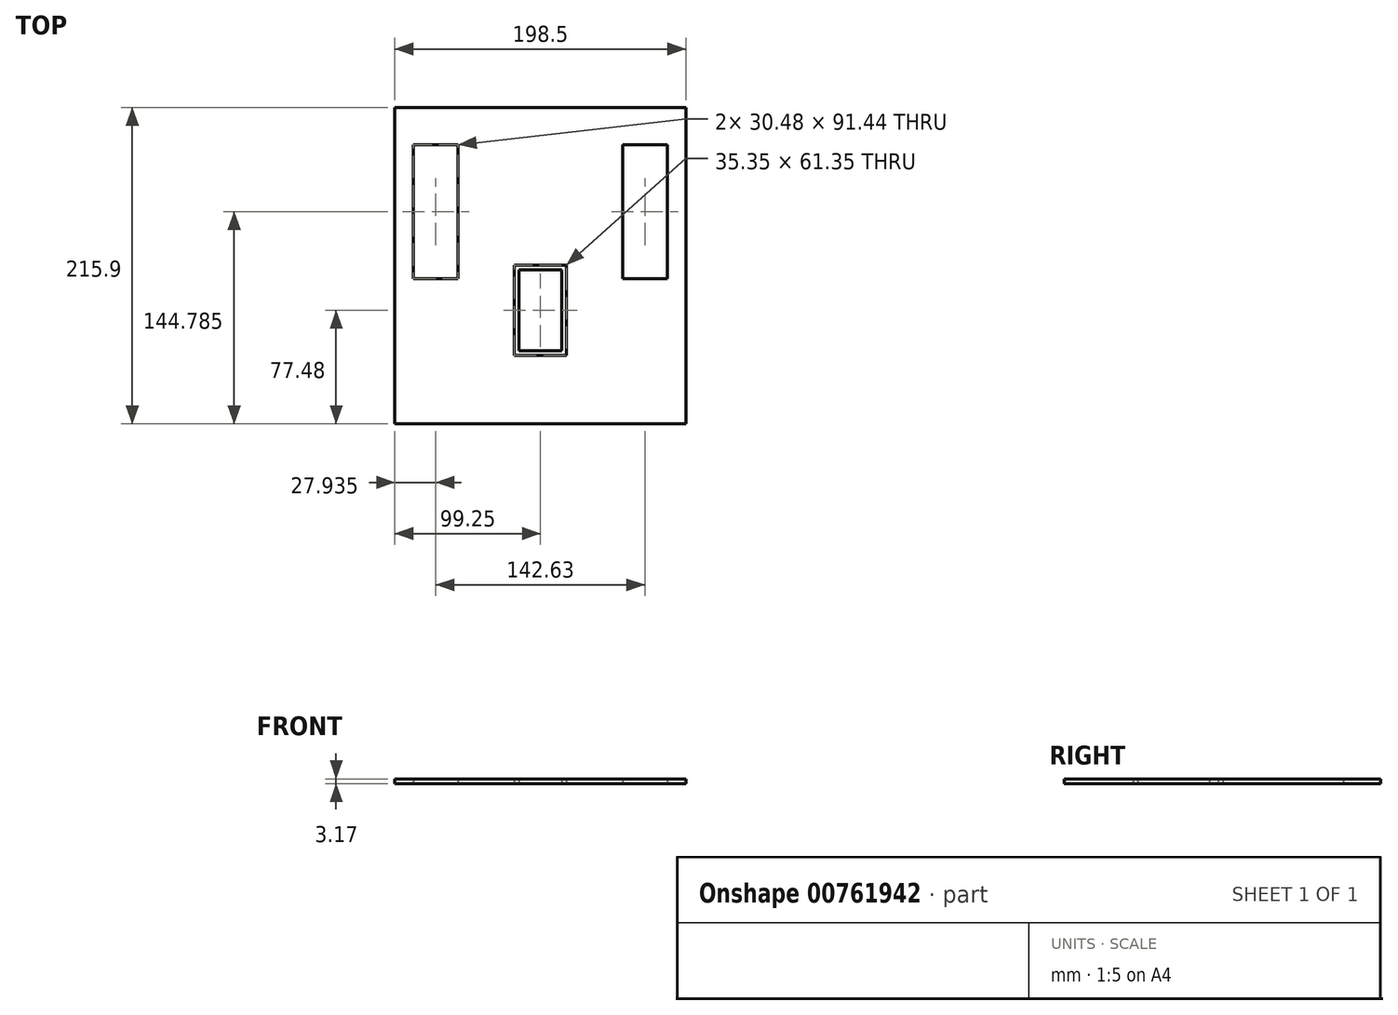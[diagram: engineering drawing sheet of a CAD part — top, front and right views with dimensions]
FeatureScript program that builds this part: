
annotation { "Feature Type Name" : "Feature", "Feature Type Description" : "" }
export const myFeature = defineFeature(function(context is Context, id is Id, definition is map)
    precondition{}
    {
        {
            var Q0;
            Q0=qCreatedBy(makeId("Top.planeOp"),FACE);
            var sketch = newSketch(context, id + "F0", { "sketchPlane" : qUnion([Q0])});
            skLineSegment(sketch, "E0", {"start": v(-27.5, 0) * mm, "end": v(-27.5, 38) * mm});
            skLineSegment(sketch, "E1", {"start": v(27.5, 38) * mm, "end": v(-27.5, 38) * mm});
            skLineSegment(sketch, "E2", {"start": v(27.5, 38) * mm, "end": v(27.5, -38) * mm});
            skLineSegment(sketch, "E3", {"start": v(27.5, -38) * mm, "end": v(-27.5, -38) * mm});
            skLineSegment(sketch, "E4", {"start": v(-27.5, 0) * mm, "end": v(-27.5, -38) * mm});
            skLineSegment(sketch, "E5", {"start": v(-30.68, 38) * mm, "end": v(-30.68, 41.18) * mm});
            skLineSegment(sketch, "E6", {"start": v(-30.68, 41.18) * mm, "end": v(-27.5, 41.18) * mm});
            skLineSegment(sketch, "E7", {"start": v(-27.5, -41.17) * mm, "end": v(-30.68, -41.17) * mm});
            skLineSegment(sketch, "E8", {"start": v(-30.68, -41.17) * mm, "end": v(-30.68, 38) * mm});
            skLineSegment(sketch, "E9", {"start": v(-27.5, 41.18) * mm, "end": v(27.5, 41.18) * mm});
            skLineSegment(sketch, "E10", {"start": v(27.5, 41.18) * mm, "end": v(30.68, 41.18) * mm});
            skLineSegment(sketch, "E11", {"start": v(30.68, -38) * mm, "end": v(30.68, 41.18) * mm});
            skLineSegment(sketch, "E12", {"start": v(30.68, -38) * mm, "end": v(30.68, -41.17) * mm});
            skLineSegment(sketch, "E13", {"start": v(30.68, -41.17) * mm, "end": v(-27.5, -41.17) * mm});
            skLineSegment(sketch, "E14", {"start": v(-27.5, -41.17) * mm, "end": v(27.5, -41.17) * mm});
            skLineSegment(sketch, "E15", {"start": v(-27.5, -41.17) * mm, "end": v(0, -41.17) * mm});
            skLineSegment(sketch, "E16", {"start": v(0, -41.17) * mm, "end": v(14.5, -41.17) * mm});
            skLineSegment(sketch, "E17", {"start": v(14.5, -41.17) * mm, "end": v(0, -41.17) * mm});
            skLineSegment(sketch, "E18", {"start": v(0, -41.17) * mm, "end": v(-13.75, -41.17) * mm});
            skLineSegment(sketch, "E19", {"start": v(0, -41.17) * mm, "end": v(-14.5, -41.17) * mm});
            skLineSegment(sketch, "E20", {"start": v(-14.5, -44.35) * mm, "end": v(-14.5, -96.17) * mm});
            skLineSegment(sketch, "E21", {"start": v(14.5, -96.17) * mm, "end": v(14.5, -44.35) * mm});
            skLineSegment(sketch, "E22", {"start": v(14.5, -96.17) * mm, "end": v(14.5, -99.35) * mm});
            skLineSegment(sketch, "E23", {"start": v(14.5, -99.35) * mm, "end": v(-14.5, -99.35) * mm});
            skLineSegment(sketch, "E24", {"start": v(-17.67, -99.35) * mm, "end": v(-17.67, -41.17) * mm});
            skLineSegment(sketch, "E25", {"start": v(14.5, -44.35) * mm, "end": v(-14.5, -44.35) * mm});
            skLineSegment(sketch, "E26", {"start": v(14.5, -41.17) * mm, "end": v(17.68, -41.17) * mm});
            skLineSegment(sketch, "E27", {"start": v(17.68, -99.35) * mm, "end": v(17.68, -41.17) * mm});
            skLineSegment(sketch, "E28", {"start": v(-17.67, -99.35) * mm, "end": v(-17.67, -102.53) * mm});
            skLineSegment(sketch, "E29", {"start": v(-17.67, -102.53) * mm, "end": v(17.68, -102.53) * mm});
            skLineSegment(sketch, "E30", {"start": v(17.68, -102.53) * mm, "end": v(17.68, -99.35) * mm});
            skLineSegment(sketch, "E31", {"start": v(-14.5, -96.17) * mm, "end": v(-14.5, -99.35) * mm});
            skLineSegment(sketch, "E32", {"start": v(-30.68, 41.18) * mm, "end": v(-56.08, 41.18) * mm});
            skLineSegment(sketch, "E33", {"start": v(-56.08, 41.18) * mm, "end": v(-86.55, 41.18) * mm});
            skLineSegment(sketch, "E34", {"start": v(-86.55, 41.18) * mm, "end": v(-86.55, -50.27) * mm});
            skLineSegment(sketch, "E35", {"start": v(-56.07, -50.27) * mm, "end": v(-86.55, -50.27) * mm});
            skLineSegment(sketch, "E36", {"start": v(-56.07, -50.27) * mm, "end": v(-56.08, 41.18) * mm});
            skLineSegment(sketch, "E37", {"start": v(30.68, 41.18) * mm, "end": v(56.08, 41.18) * mm});
            skLineSegment(sketch, "E38", {"start": v(56.08, 41.18) * mm, "end": v(86.56, 41.18) * mm});
            skLineSegment(sketch, "E39", {"start": v(86.56, 41.18) * mm, "end": v(86.56, -50.27) * mm});
            skLineSegment(sketch, "E40", {"start": v(86.56, -50.27) * mm, "end": v(56.08, -50.27) * mm});
            skLineSegment(sketch, "E41", {"start": v(56.08, -50.27) * mm, "end": v(56.08, 41.18) * mm});
            skLineSegment(sketch, "E42", {"start": v(-86.55, 41.18) * mm, "end": v(-86.55, 66.57) * mm});
            skLineSegment(sketch, "E43", {"start": v(-86.55, 66.57) * mm, "end": v(-86.55, 41.18) * mm});
            skLineSegment(sketch, "E44", {"start": v(86.56, 41.18) * mm, "end": v(86.56, 66.58) * mm});
            skLineSegment(sketch, "E45", {"start": v(86.56, 66.58) * mm, "end": v(99.26, 66.58) * mm});
            skLineSegment(sketch, "E46", {"start": v(-86.55, 66.57) * mm, "end": v(-99.26, 66.57) * mm});
            skLineSegment(sketch, "E47", {"start": v(-99.26, 66.57) * mm, "end": v(-99.26, -149.32) * mm});
            skLineSegment(sketch, "E48", {"start": v(-99.26, -149.32) * mm, "end": v(-99.26, 66.57) * mm});
            skLineSegment(sketch, "E49", {"start": v(99.26, 66.58) * mm, "end": v(99.26, -149.32) * mm});
            skLineSegment(sketch, "E50", {"start": v(99.26, -149.32) * mm, "end": v(-99.25, -149.32) * mm});
            skLineSegment(sketch, "E51", {"start": v(-86.55, 66.57) * mm, "end": v(86.56, 66.58) * mm});
            skSolve(sketch);
        }
        {
            var Q0;
            Q0 = qSketchRegion(id + "F0", true);
            var Q1;
            Q1=makeQuery(id+"F0.imprint","IMPRINT",FACE,{"disambiguationData":[TD([[makeQuery(id+"F0.imprint","IMPRINT",EDGE,{"derivedFrom":sQuery(id+"F0.wireOp",EDGE,"E0")}),-1.0]])]});
            var Q2;
            Q2=makeQuery(id+"F0.imprint","IMPRINT",FACE,{"disambiguationData":[TD([[makeQuery(id+"F0.imprint","IMPRINT",EDGE,{"derivedFrom":sQuery(id+"F0.wireOp",EDGE,"E20")}),1.0]])]});
            var Q3;
            {var subQ4=sQuery(id+"F0.wireOp",EDGE,"E17");Q3=makeQuery(id+"F0.imprint","IMPRINT",FACE,{"disambiguationData":[TD([[makeQuery(id+"F0.imprint","IMPRINT",EDGE,{"derivedFrom":subQ4}),1.0]])]});}
            var Q4;
            Q4=makeQuery(id+"F0.imprint","IMPRINT",FACE,{"disambiguationData":[TD([[makeQuery(id+"F0.imprint","IMPRINT",EDGE,{"derivedFrom":sQuery(id+"F0.wireOp",EDGE,"E0")}),1.0]])]});
            extrude(context, id + "F1", {"entities" : qUnion([Q0, Q1, Q2, Q3, Q4]), "depth" : 3.17 * mm, "offsetDistance" : 25.4 * mm});
        }
    });
